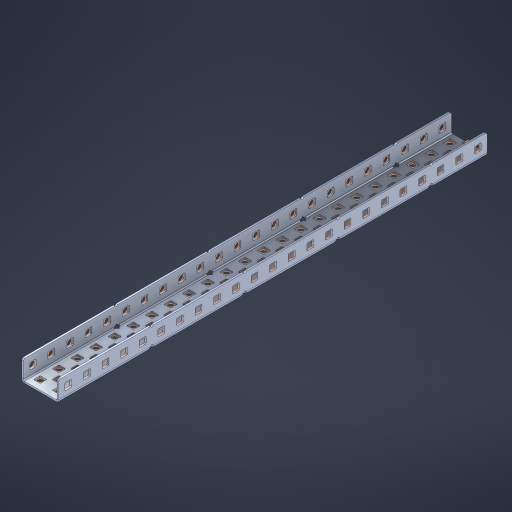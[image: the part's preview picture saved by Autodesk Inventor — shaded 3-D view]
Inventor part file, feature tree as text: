
AUTODESK INVENTOR PART (.ipt)
format: ipt  version: 2023 (Build 270158000, 158)  size: 1,554,944 bytes
history: native  units: in
note: dims shown in document units (in); Inventor stores cm internally (conversion verified against a paired STEP export)
features: other x122, extrude x113, sheet_metal_op x11, sketch x10, pattern_linear x2, mirror x1, chamfer x1
ambient origin geometry x8: Origin, YZ Plane, XZ Plane, XY Plane, X Axis, Y Axis, Z Axis, Center Point
bodies: Solid1 (feature_tree), Body (feature_tree)
feature tree (260):
  sheet_metal_op  "Flanges"
  other  "Flange Pattern Plane"
  other  "Flange Pattern Sketch"
  sheet_metal_op  "Flange Pattern"
  sheet_metal_op  "Body Pattern"
  pattern_linear  "Center Pattern"  Spacing1=0.0469in  [1 undecoded]
  other  "Arc Length"
  mirror  "Notch Mirror"
  pattern_linear  "Notch Pattern"  Spacing1=0.182in  [1 undecoded]
  chamfer  "End Chamfer"
  extrude  "Half Cut"  Depth=0.02in
  sketch  "Sketch1"  dims[d0=1.0in]
  other  "Plate1"
  sketch  "Sketch2"  dims[d1=11.5in]
  other  "Plate2"
  sheet_metal_op  "Bend1"
  sheet_metal_op  "Corner1"
  sketch  "Sketch3"  dims[d2=0.0469in]
  sketch  "Sketch7"  dims[d3=0.0469in]
  other  "Srf1"
  other  "Srf2"
  sketch  "Sketch8"  dims[d4=0.0234in]
  sketch  "Sketch9"  dims[d5=0.0938in]
  other  "Srf91"
  sheet_metal_op  "Body Pattern Sketch"
  other  "Srf92"
  sketch  "Sketch13"  dims[d6=0.0469in]
  sketch  "Sketch14"  dims[d7=0.5in d8=90.0deg d9=0.0312in]
  sketch  "Sketch15"  dims[d10=0.1875in]
  sketch  "Sketch16"  dims[d11=0.0469in d12=0.0469in d16=0.182in d17=0.02in d18=0.0469in d19=0.0in d20=0.25in d21=0.25in d38=9.0551in d40=0.5in d41=0.7874in d43=1.0in d46=0.172in d47=1.0in d48=0.0in d49=0.182in d50=0.02in d51=0.25in d52=0.25in d53=0.0469in d54=0.0in d55=0.172in d56=1.0in d57=0.0in d58=0.25in d60=9.0551in d62=0.5in d63=0.7874in d65=0.5in d85=0.1227in d86=0.1659in d88=0.04in d89=0.0469in d90=0.0in d91=0.04in d92=0.0491in d95=2.5in d96=0.04in d97=0.25in d98=45.0deg d99=0.25in d100=0.5in d101=0.0in d102=2.497in d106=0.182in d107=0.02in d108=0.5in d109=0.5in d110=0.0469in d111=0.0in d112=0.172in d113=0.5in d114=0.0in d117=0.5in d118=0.5in d119=0.5in]
  other  "Srf786"
  other  "Srf823"
  other  "Srf824"
  other  "Srf825"
  other  "Srf826"
  other  "Srf827"
  other  "Srf828"
  other  "Srf829"
  other  "Srf856"
  other  "Srf857"
  other  "Srf858"
  other  "Srf859"
  other  "Srf860"
  other  "Srf861"
  other  "Srf862"
  other  "Srf889"
  other  "Srf890"
  other  "Srf891"
  other  "Srf892"
  other  "Srf893"
  other  "Srf894"
  other  "Srf895"
  other  "Srf896"
  other  "Srf922"
  other  "Srf923"
  other  "Srf924"
  other  "Srf925"
  other  "Srf926"
  other  "Srf959"
  other  "Srf960"
  other  "Srf961"
  other  "Srf962"
  other  "Srf963"
  other  "Srf996"
  other  "Srf997"
  other  "Srf998"
  other  "Srf999"
  other  "Srf1000"
  other  "Srf1143"
  other  "Srf1144"
  other  "Srf1145"
  other  "Srf1146"
  other  "Srf1147"
  other  "Srf1148"
  other  "Srf1149"
  other  "Srf1150"
  other  "Srf1151"
  other  "Srf1152"
  other  "Srf1153"
  other  "Srf1154"
  other  "Srf1155"
  other  "Srf1156"
  other  "Srf1157"
  other  "Srf1158"
  other  "Srf1159"
  other  "Srf1160"
  other  "Srf1161"
  other  "Srf1162"
  other  "Srf1163"
  other  "Srf1164"
  other  "Srf1165"
  other  "Srf1166"
  other  "Srf1167"
  other  "Srf1168"
  other  "Srf1169"
  other  "Srf1170"
  other  "Srf1171"
  other  "Srf1172"
  other  "Srf1173"
  other  "Srf1174"
  other  "Srf1199"
  other  "Srf1200"
  other  "Srf1201"
  other  "Srf1202"
  other  "Srf1203"
  other  "Srf1204"
  other  "Srf1205"
  other  "Srf1206"
  other  "Srf1207"
  other  "Srf1208"
  other  "Srf1209"
  other  "Srf1210"
  other  "Srf1211"
  other  "Srf1212"
  other  "Srf1213"
  other  "Srf1214"
  other  "Srf1215"
  other  "Srf1216"
  other  "Srf1217"
  other  "Srf1218"
  other  "Srf1219"
  other  "Srf1220"
  other  "Srf1221"
  other  "Srf1222"
  other  "Srf1223"
  other  "Srf1224"
  other  "Srf1225"
  other  "Srf1226"
  other  "Srf1227"
  other  "Srf1228"
  other  "Srf1229"
  other  "Srf1230"
  other  "Srf1255"
  other  "Srf1256"
  other  "Srf1257"
  other  "Srf1258"
  other  "Srf1259"
  other  "Srf1260"
  other  "Srf1261"
  other  "Srf1262"
  other  "Srf1263"
  sheet_metal_op  "Flange Stamp"
  sheet_metal_op  "Flange Circle"
  sheet_metal_op  "Body Stamp"
  sheet_metal_op  "Body Circle"
  other  "Center Stamp"
  other  "Center Circle"
  sheet_metal_op  "Notch"
  extrude  "ExtrusionSrf2"  Depth=0.0469in
  extrude  "ExtrusionSrf92"  TaperAngle=0.0deg  [1 undecoded]
  extrude  "ExtrusionSrf823"  Depth=0.5in
  extrude  "ExtrusionSrf824"  Depth=0.5in
  extrude  "ExtrusionSrf825"  Depth=0.5in
  extrude  "ExtrusionSrf826"  Depth=0.5in
  extrude  "ExtrusionSrf827"  Depth=1.0in TaperAngle=0.0deg
  extrude  "ExtrusionSrf828"  Depth=0.5in
  extrude  "ExtrusionSrf829"  Depth=0.02in
  extrude  "ExtrusionSrf856"  Depth=0.5in
  extrude  "ExtrusionSrf857"  Depth=0.5in
  extrude  "ExtrusionSrf858"  Depth=0.0469in
  extrude  "ExtrusionSrf859"  TaperAngle=0.0deg  [1 undecoded]
  extrude  "ExtrusionSrf860"  Depth=0.5in
  extrude  "ExtrusionSrf861"  Depth=1.0in TaperAngle=0.0deg
  extrude  "ExtrusionSrf862"  Depth=0.5in
  extrude  "ExtrusionSrf889"  Depth=0.5in
  extrude  "ExtrusionSrf890"  Depth=0.5in
  extrude  "ExtrusionSrf891"  Depth=0.5in
  extrude  "ExtrusionSrf892"  Depth=0.5in
  extrude  "ExtrusionSrf893"  Depth=0.5in
  extrude  "ExtrusionSrf894"  Depth=0.0469in
  extrude  "ExtrusionSrf895"  TaperAngle=0.0deg  [1 undecoded]
  extrude  "ExtrusionSrf896"  Depth=0.5in
  extrude  "ExtrusionSrf922"  Depth=0.5in
  extrude  "ExtrusionSrf923"  Depth=2.5in
  extrude  "ExtrusionSrf924"  Depth=0.5in TaperAngle=45.0deg
  extrude  "ExtrusionSrf925"  Depth=0.5in
  extrude  "ExtrusionSrf926"  Depth=0.5in TaperAngle=0.0deg
  extrude  "ExtrusionSrf959"  Depth=0.5in
  extrude  "ExtrusionSrf960"  Depth=0.5in
  extrude  "ExtrusionSrf961"  Depth=0.02in
  extrude  "ExtrusionSrf962"  Depth=0.5in
  extrude  "ExtrusionSrf963"  Depth=0.5in
  extrude  "ExtrusionSrf996"  Depth=0.0469in
  extrude  "ExtrusionSrf997"  TaperAngle=0.0deg  [1 undecoded]
  extrude  "ExtrusionSrf998"  Depth=0.5in
  extrude  "ExtrusionSrf999"  Depth=0.5in TaperAngle=0.0deg
  extrude  "ExtrusionSrf1000"  Depth=0.5in
  extrude  "ExtrusionSrf1143"  Depth=0.5in
  extrude  "ExtrusionSrf1144"  Depth=0.5in
  extrude  "ExtrusionSrf1145"  [1 undecoded]
  extrude  "ExtrusionSrf1146"  [1 undecoded]
  extrude  "ExtrusionSrf1147"  [1 undecoded]
  extrude  "ExtrusionSrf1148"  [1 undecoded]
  extrude  "ExtrusionSrf1149"  [1 undecoded]
  extrude  "ExtrusionSrf1150"  [1 undecoded]
  extrude  "ExtrusionSrf1151"  [1 undecoded]
  extrude  "ExtrusionSrf1152"  [1 undecoded]
  extrude  "ExtrusionSrf1153"  [1 undecoded]
  extrude  "ExtrusionSrf1154"  [1 undecoded]
  extrude  "ExtrusionSrf1155"  [1 undecoded]
  extrude  "ExtrusionSrf1156"  [1 undecoded]
  extrude  "ExtrusionSrf1157"  [1 undecoded]
  extrude  "ExtrusionSrf1158"  [1 undecoded]
  extrude  "ExtrusionSrf1159"  [1 undecoded]
  extrude  "ExtrusionSrf1160"  [1 undecoded]
  extrude  "ExtrusionSrf1161"  [1 undecoded]
  extrude  "ExtrusionSrf1162"  [1 undecoded]
  extrude  "ExtrusionSrf1163"  [1 undecoded]
  extrude  "ExtrusionSrf1164"  [1 undecoded]
  extrude  "ExtrusionSrf1165"  [1 undecoded]
  extrude  "ExtrusionSrf1166"  [1 undecoded]
  extrude  "ExtrusionSrf1167"  [1 undecoded]
  extrude  "ExtrusionSrf1168"  [1 undecoded]
  extrude  "ExtrusionSrf1169"  [1 undecoded]
  extrude  "ExtrusionSrf1170"  [1 undecoded]
  extrude  "ExtrusionSrf1171"  [1 undecoded]
  extrude  "ExtrusionSrf1172"  [1 undecoded]
  extrude  "ExtrusionSrf1173"  [1 undecoded]
  extrude  "ExtrusionSrf1174"  [1 undecoded]
  extrude  "ExtrusionSrf1199"  [1 undecoded]
  extrude  "ExtrusionSrf1200"  [1 undecoded]
  extrude  "ExtrusionSrf1201"  [1 undecoded]
  extrude  "ExtrusionSrf1202"  [1 undecoded]
  extrude  "ExtrusionSrf1203"  [1 undecoded]
  extrude  "ExtrusionSrf1204"  [1 undecoded]
  extrude  "ExtrusionSrf1205"  [1 undecoded]
  extrude  "ExtrusionSrf1206"  [1 undecoded]
  extrude  "ExtrusionSrf1207"  [1 undecoded]
  extrude  "ExtrusionSrf1208"  [1 undecoded]
  extrude  "ExtrusionSrf1209"  [1 undecoded]
  extrude  "ExtrusionSrf1210"  [1 undecoded]
  extrude  "ExtrusionSrf1211"  [1 undecoded]
  extrude  "ExtrusionSrf1212"  [1 undecoded]
  extrude  "ExtrusionSrf1213"  [1 undecoded]
  extrude  "ExtrusionSrf1214"  [1 undecoded]
  extrude  "ExtrusionSrf1215"  [1 undecoded]
  extrude  "ExtrusionSrf1216"  [1 undecoded]
  extrude  "ExtrusionSrf1217"  [1 undecoded]
  extrude  "ExtrusionSrf1218"  [1 undecoded]
  extrude  "ExtrusionSrf1219"  [1 undecoded]
  extrude  "ExtrusionSrf1220"  [1 undecoded]
  extrude  "ExtrusionSrf1221"  [1 undecoded]
  extrude  "ExtrusionSrf1222"  [1 undecoded]
  extrude  "ExtrusionSrf1223"  [1 undecoded]
  extrude  "ExtrusionSrf1224"  [1 undecoded]
  extrude  "ExtrusionSrf1225"  [1 undecoded]
  extrude  "ExtrusionSrf1226"  [1 undecoded]
  extrude  "ExtrusionSrf1227"  [1 undecoded]
  extrude  "ExtrusionSrf1228"  [1 undecoded]
  extrude  "ExtrusionSrf1229"  [1 undecoded]
  extrude  "ExtrusionSrf1230"  [1 undecoded]
  extrude  "ExtrusionSrf1255"  [1 undecoded]
  extrude  "ExtrusionSrf1256"  [1 undecoded]
  extrude  "ExtrusionSrf1257"  [1 undecoded]
  extrude  "ExtrusionSrf1258"  [1 undecoded]
  extrude  "ExtrusionSrf1259"  [1 undecoded]
  extrude  "ExtrusionSrf1260"  [1 undecoded]
  extrude  "ExtrusionSrf1261"  [1 undecoded]
  extrude  "ExtrusionSrf1262"  [1 undecoded]
  extrude  "ExtrusionSrf1263"  [1 undecoded]
note: 77 required parameter values undecoded (feature->parameter linkage not recoverable at this tier; creation-order binding heuristic only, values carry confidence <= 0.55)
